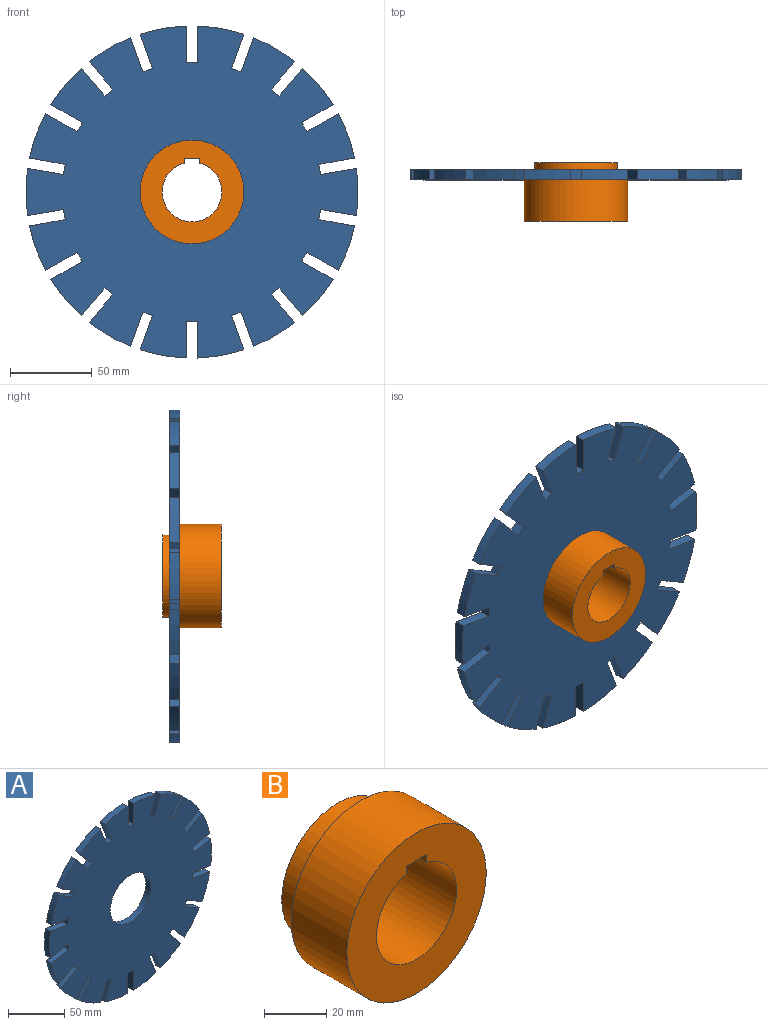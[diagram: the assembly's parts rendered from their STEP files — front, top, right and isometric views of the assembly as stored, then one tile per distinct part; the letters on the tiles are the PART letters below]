
ASSEMBLY  parts=2 mates=1
PART A: 75 faces, bbox 203.2x6.4x203.1 mm
  f0: plane 17.03x14.29mm, normal (-0.77,0,0.64), area 141.1mm2, adj f1,f72,f73,f74
  f1: cylinder r=101.6mm len=25.13mm, axis (0,1,0), area 184.9mm2, adj f0,f2,f73,f74
  f2: plane 20.88x7.6mm, normal (0.94,0,-0.34), area 141.1mm2, adj f1,f3,f73,f74
  f3: plane 6.35x5.97mm, normal (-0.34,0,-0.94), area 40.3mm2, adj f2,f4,f73,f74
  f4: plane 20.88x7.6mm, normal (-0.94,0,0.34), area 141.1mm2, adj f3,f5,f73,f74
  f5: cylinder r=101.6mm len=28.57mm, axis (0,1,0), area 184.9mm2, adj f4,f6,f73,f74
  f6: plane 22.23x6.35mm, normal (1,0,0), area 141.1mm2, adj f5,f7,f73,f74
  f7: plane 6.35x6.35mm, normal (0,0,-1), area 40.3mm2, adj f6,f8,f73,f74
  f8: plane 22.23x6.35mm, normal (-1,0,0), area 141.1mm2, adj f7,f9,f73,f74
  f9: cylinder r=101.6mm len=28.57mm, axis (0,1,0), area 184.9mm2, adj f8,f10,f73,f74
  f10: plane 20.88x7.6mm, normal (0.94,0,0.34), area 141.1mm2, adj f9,f11,f73,f74
  f11: plane 6.35x5.97mm, normal (0.34,0,-0.94), area 40.3mm2, adj f10,f12,f73,f74
  f12: plane 20.88x7.6mm, normal (-0.94,0,-0.34), area 141.1mm2, adj f11,f13,f73,f74
  f13: cylinder r=101.6mm len=25.13mm, axis (0,1,0), area 184.9mm2, adj f12,f14,f73,f74
  f14: plane 17.03x14.29mm, normal (0.77,0,0.64), area 141.1mm2, adj f13,f15,f73,f74
  f15: plane 6.35x4.86mm, normal (0.64,0,-0.77), area 40.3mm2, adj f14,f16,f73,f74
  f16: plane 17.03x14.29mm, normal (-0.77,0,-0.64), area 141.1mm2, adj f15,f17,f73,f74
  f17: cylinder r=101.6mm len=22.23mm, axis (0,1,0), area 184.9mm2, adj f16,f18,f73,f74
  f18: plane 19.25x11.11mm, normal (0.5,0,0.87), area 141.1mm2, adj f17,f19,f73,f74
  f19: plane 6.35x5.5mm, normal (0.87,0,-0.5), area 40.3mm2, adj f18,f20,f73,f74
  f20: plane 19.25x11.11mm, normal (-0.5,0,-0.87), area 141.1mm2, adj f19,f21,f73,f74
  f21: cylinder r=101.6mm len=27.26mm, axis (0,1,0), area 184.9mm2, adj f20,f22,f73,f74
  f22: plane 21.89x6.35mm, normal (0.17,0,0.98), area 141.1mm2, adj f21,f23,f73,f74
  f23: plane 6.35x6.25mm, normal (0.98,0,-0.17), area 40.3mm2, adj f22,f24,f73,f74
  f24: plane 21.89x6.35mm, normal (-0.17,0,-0.98), area 141.1mm2, adj f23,f25,f73,f74
  f25: cylinder r=101.6mm len=29.01mm, axis (0,1,0), area 184.9mm2, adj f24,f26,f73,f74
  f26: plane 21.89x6.35mm, normal (-0.17,0,0.98), area 141.1mm2, adj f25,f27,f73,f74
  f27: plane 6.35x6.25mm, normal (0.98,0,0.17), area 40.3mm2, adj f26,f28,f73,f74
  f28: plane 21.89x6.35mm, normal (0.17,0,-0.98), area 141.1mm2, adj f27,f29,f73,f74
  f29: cylinder r=101.6mm len=27.27mm, axis (0,1,0), area 184.9mm2, adj f28,f30,f73,f74
  f30: plane 19.25x11.11mm, normal (-0.5,0,0.87), area 141.1mm2, adj f29,f31,f73,f74
  f31: plane 6.35x5.5mm, normal (0.87,0,0.5), area 40.3mm2, adj f30,f32,f73,f74
  f32: plane 19.25x11.11mm, normal (0.5,0,-0.87), area 141.1mm2, adj f31,f33,f73,f74
  f33: cylinder r=101.6mm len=22.23mm, axis (0,1,0), area 184.9mm2, adj f32,f34,f73,f74
  f34: plane 17.03x14.29mm, normal (-0.77,0,0.64), area 141.1mm2, adj f33,f35,f73,f74
  f35: plane 6.35x4.86mm, normal (0.64,0,0.77), area 40.3mm2, adj f34,f36,f73,f74
  f36: plane 17.03x14.29mm, normal (0.77,0,-0.64), area 141.1mm2, adj f35,f37,f73,f74
  f37: cylinder r=101.6mm len=25.13mm, axis (0,1,0), area 184.9mm2, adj f36,f38,f73,f74
  f38: plane 20.88x7.6mm, normal (-0.94,0,0.34), area 141.1mm2, adj f37,f39,f73,f74
  f39: plane 6.35x5.97mm, normal (0.34,0,0.94), area 40.3mm2, adj f38,f40,f73,f74
  f40: plane 20.88x7.6mm, normal (0.94,0,-0.34), area 141.1mm2, adj f39,f41,f73,f74
  f41: cylinder r=101.6mm len=28.57mm, axis (0,1,0), area 184.9mm2, adj f40,f42,f73,f74
  f42: plane 22.23x6.35mm, normal (-1,0,0), area 141.1mm2, adj f41,f43,f73,f74
  f43: plane 6.35x6.35mm, normal (0,0,1), area 40.3mm2, adj f42,f44,f73,f74
  f44: plane 22.23x6.35mm, normal (1,0,0), area 141.1mm2, adj f43,f45,f73,f74
  f45: cylinder r=101.6mm len=28.57mm, axis (0,1,0), area 184.9mm2, adj f44,f46,f73,f74
  f46: plane 20.88x7.6mm, normal (-0.94,0,-0.34), area 141.1mm2, adj f45,f47,f73,f74
  f47: plane 6.35x5.97mm, normal (-0.34,0,0.94), area 40.3mm2, adj f46,f48,f73,f74
  f48: plane 20.88x7.6mm, normal (0.94,0,0.34), area 141.1mm2, adj f47,f49,f73,f74
  f49: cylinder r=101.6mm len=25.13mm, axis (0,1,0), area 184.9mm2, adj f48,f50,f73,f74
  f50: plane 17.03x14.29mm, normal (-0.77,0,-0.64), area 141.1mm2, adj f49,f51,f73,f74
  f51: plane 6.35x4.86mm, normal (-0.64,0,0.77), area 40.3mm2, adj f50,f52,f73,f74
  f52: plane 17.03x14.29mm, normal (0.77,0,0.64), area 141.1mm2, adj f51,f53,f73,f74
  f53: cylinder r=101.6mm len=22.23mm, axis (0,1,0), area 184.9mm2, adj f52,f54,f73,f74
  f54: plane 19.25x11.11mm, normal (-0.5,0,-0.87), area 141.1mm2, adj f53,f55,f73,f74
  f55: plane 6.35x5.5mm, normal (-0.87,0,0.5), area 40.3mm2, adj f54,f56,f73,f74
  f56: plane 19.25x11.11mm, normal (0.5,0,0.87), area 141.1mm2, adj f55,f57,f73,f74
  f57: cylinder r=101.6mm len=27.26mm, axis (0,1,0), area 184.9mm2, adj f56,f58,f73,f74
  f58: plane 21.89x6.35mm, normal (-0.17,0,-0.98), area 141.1mm2, adj f57,f59,f73,f74
  f59: plane 6.35x6.25mm, normal (-0.98,0,0.17), area 40.3mm2, adj f58,f60,f73,f74
  f60: plane 21.89x6.35mm, normal (0.17,0,0.98), area 141.1mm2, adj f59,f61,f73,f74
  f61: cylinder r=101.6mm len=29.01mm, axis (0,1,0), area 184.9mm2, adj f60,f62,f73,f74
  f62: plane 21.89x6.35mm, normal (0.17,0,-0.98), area 141.1mm2, adj f61,f63,f73,f74
  f63: plane 6.35x6.25mm, normal (-0.98,0,-0.17), area 40.3mm2, adj f62,f64,f73,f74
  f64: plane 21.89x6.35mm, normal (-0.17,0,0.98), area 141.1mm2, adj f63,f65,f73,f74
  f65: cylinder r=101.6mm len=27.27mm, axis (0,1,0), area 184.9mm2, adj f64,f66,f73,f74
  f66: plane 19.25x11.11mm, normal (0.5,0,-0.87), area 141.1mm2, adj f65,f67,f73,f74
  f67: plane 6.35x5.5mm, normal (-0.87,0,-0.5), area 40.3mm2, adj f66,f68,f73,f74
  f68: plane 19.25x11.11mm, normal (-0.5,0,0.87), area 141.1mm2, adj f67,f69,f73,f74
  f69: cylinder r=101.6mm len=22.23mm, axis (0,1,0), area 184.9mm2, adj f68,f70,f73,f74
  f70: plane 17.03x14.29mm, normal (0.77,0,-0.64), area 141.1mm2, adj f69,f72,f73,f74
  f71: cylinder r=25.4mm len=50.8mm, axis (0,1,0), area 1013.4mm2, adj f73,f74
  f72: plane 6.35x4.86mm, normal (-0.64,0,-0.77), area 40.3mm2, adj f0,f70,f73,f74
  f73: plane 203.2x203.1mm, normal (0,-1,0), area 27858.3mm2, adj f0,f1,f2,f3,f4,f5,f6,f7
  f74: plane 203.2x203.1mm, normal (0,1,0), area 27858.3mm2, adj f0,f1,f2,f3,f4,f5,f6,f7
PART B: 9 faces, bbox 63.5x36x63.5 mm
  f0: plane 35.99x3.18mm, normal (1,0,0), area 114.3mm2, adj f1,f3,f5,f7
  f1: plane 35.99x9.53mm, normal (0,0,-1), area 342.8mm2, adj f0,f2,f5,f7
  f2: plane 35.99x3.18mm, normal (-1,0,0), area 114.3mm2, adj f1,f3,f5,f7
  f3: cylinder r=18.26mm len=36.51mm, axis (0,1,0), area 3781.7mm2, adj f0,f2,f5,f7
  f4: cylinder r=25.4mm len=50.8mm, axis (0,1,0), area 1690.4mm2, adj f5,f8
  f5: plane 50.8x50.8mm, normal (0,1,0), area 953.6mm2, adj f0,f1,f2,f3,f4
  f6: cylinder r=31.75mm len=63.5mm, axis (0,1,0), area 5067.1mm2, adj f7,f8
  f7: plane 63.5x63.5mm, normal (0,-1,0), area 2093.6mm2, adj f0,f1,f2,f3,f6
  f8: plane 63.5x63.5mm, normal (0,1,0), area 1140.1mm2, adj f4,f6
PLACE A t=(-0.68,15.17,2.71)mm
PLACE B t=(-0.68,19.41,2.71)mm
MATE fastened A.f69 <-> B.f6  axis (0,-1,0) through (-0.68,8.82,2.71)mm
